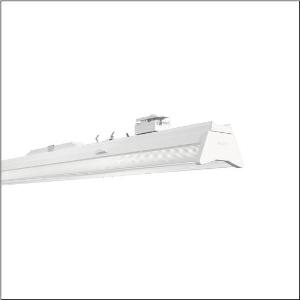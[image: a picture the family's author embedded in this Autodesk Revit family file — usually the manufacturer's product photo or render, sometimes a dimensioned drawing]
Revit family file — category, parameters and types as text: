
# Revit family: licross_r__21_performance_mo_52tm16cn445g_ee6e
name_source: partatom
category: Lighting Fixtures
units: mm (PartAtom-declared; Revit-internal decimal feet)

## family parameters
Cut with Voids When Loaded = No
Host = Face
Light Source = No
Part Type = Normal
Room Calculation Point = No
Round Connector Dimension = Use Diameter
Shared = No

## types (1)
- --- (1 x LED, 4500 lm, 24.1 W, 4000K)
    Apparent Load = 24 VA
    CIE Flux Codes = 66 88 96 79 100
    Color Rendering = 80
    Color Temperature = 4000K
    Default Elevation = 1800 mm
    Description = Licross® 21 Performance MO, luminaire insert, of sheet steel, galvanised, coil coated, white, length: 1.500mm, width: 120mm, height: 123mm, LED rated luminous flux: 4.500lm, light colour: 840, control gear: ON/OFF Multilumen, CLOi, control gear: ECG Multilumen, with plug, 3-pole, with phase selection, mains connection: 220..240V, AC, 50/60Hz, start of lifetime: 24W, end of service life: 28W, halogen-free wiring, primary light control with lens, of plastic, primary optical cover: cover, of PMMA, CAT 2 (L<= 3000cd/m²), light emission: direct/indirect distribution, primary light characteristic: symmetric, protection rating (complete): IP40, insulation class (complete): insulation class I (protective earthing), certification: CE, ENEC, UKCA, protection symbol: D if used in an environment without relevant dust loads with corresponding accessories, impact resistance: IK06, permissible ambient temperature for indoor applications: -35..+55°C, corresponds to IFS (International Featured Standards) requirements for safety and quality in the food industry, reducing of maximum allowable ambient temperature of 5°C with ceiling mounting, LABS conformity tested according to VDMA 24364:2018-05, packaging unit: 1 piece
    Height = 114 mm
    Lamp = 1 x LED
    Lamp Light Flux = 4500 lm
    Lamp Power = 24.1 W
    Lamp count = 1
    Length = 1500 mm
    Luminous efficacy = 187 lm/W
    Manufacturer = Siteco
    ModVariant = No
    Model = 52TM16CN445G
    Mounting Place = Ceiling
    Mounting Type = Pendant
    Number of Poles = 1
    OnlyDefault = Yes
    Power Factor = 1
    Product Name = Licross® 21 Performance MO
    Product group = luminaire insert
    ProductGroupID = 901
    Protection Class = Protection class I
    Protection Degree = IP 40
    RLX_Detail_Level = 1
    RLX_Emergency_Light_Flux = 0 lm
    RLX_Emergency_Type = 0
    RLX_Emergency_Type_DB = No
    RlxData = <blob elided: 31469 chars, md5=ec355ec3>
    Socket = socket
    Standby Power = 0 W
    System Light Flux = 4500 lm
    System Power = 24 W
    Type Comments = factory setting: luminous flux: 100 % | (A | C | E) | 55 mA
    Type Image = l_1256138.jpg
    URL = http://relux.com
    VarID = @adj_000185
    Voltage = 0 V
    Weight = 0.00 kg
    Width = 120 mm

## geometry (parser evidence)
native form markers: Blend x4, Sweep x13
no freeform markers — native parametric forms only
